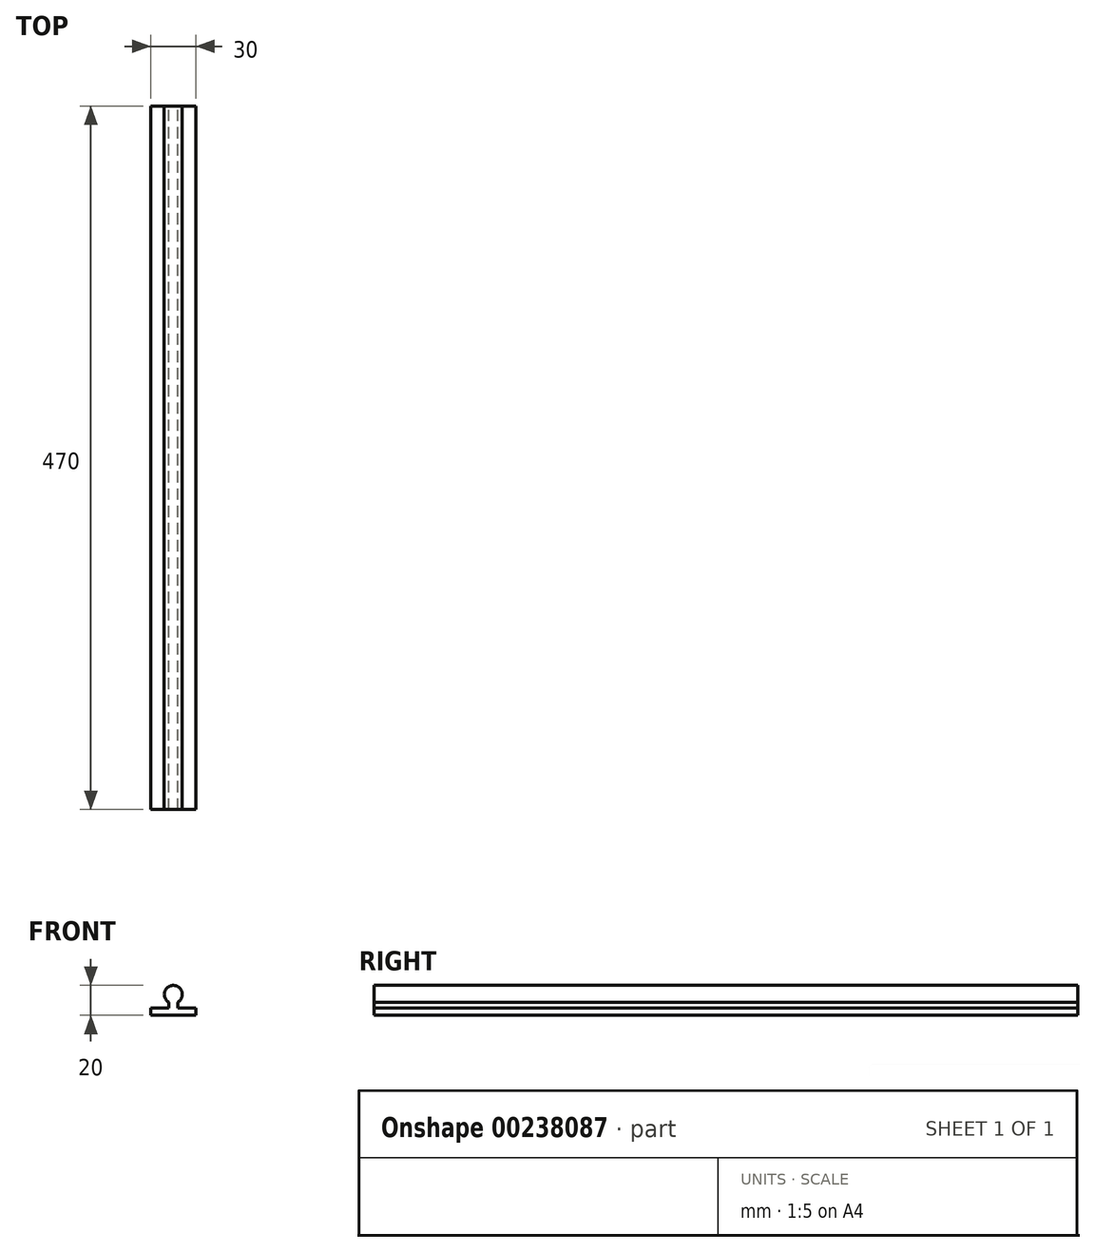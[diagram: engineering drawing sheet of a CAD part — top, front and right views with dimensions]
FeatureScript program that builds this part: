
annotation { "Feature Type Name" : "Feature", "Feature Type Description" : "" }
export const myFeature = defineFeature(function(context is Context, id is Id, definition is map)
    precondition{}
    {
        {
            var Q0;
            Q0=qCreatedBy(makeId("Front.planeOp"),FACE);
            var sketch = newSketch(context, id + "F0", { "sketchPlane" : qUnion([Q0])});
            skLineSegment(sketch, "E0", {"start": v(0, 0) * mm, "end": v(-15, 0) * mm});
            skLineSegment(sketch, "E1", {"start": v(-15, 0) * mm, "end": v(-15, 5) * mm});
            skLineSegment(sketch, "E2", {"start": v(-15, 5) * mm, "end": v(-3, 5) * mm});
            skArc(sketch, "E3", {"start": v(0, 20) * mm, "mid": v(-5.8, 15.55) * mm, "end": v(-3, 8.8) * mm});
            skLineSegment(sketch, "E4", {"start": v(-3, 5) * mm, "end": v(-3, 8.8) * mm});
            skPoint(sketch, "E5.start.orphan", {"position": v(0, 5) * mm});
            skLineSegment(sketch, "E6.MirrorCS", {"start": v(3, 5) * mm, "end": v(3, 8.8) * mm});
            skLineSegment(sketch, "E7.MirrorCS", {"start": v(15, 0) * mm, "end": v(15, 5) * mm});
            skLineSegment(sketch, "E8.MirrorCS", {"start": v(15, 5) * mm, "end": v(3, 5) * mm});
            skLineSegment(sketch, "E9.MirrorCS", {"start": v(0, 0) * mm, "end": v(15, 0) * mm});
            skArc(sketch, "E10.MirrorCS", {"start": v(0, 20) * mm, "mid": v(5.8, 15.55) * mm, "end": v(3, 8.8) * mm});
            skSolve(sketch);
        }
        {
            var Q0;
            Q0=makeQuery(id+"F0.imprint","IMPRINT",FACE,{"disambiguationData":[TD([[makeQuery(id+"F0.imprint","IMPRINT",EDGE,{"derivedFrom":sQuery(id+"F0.wireOp",EDGE,"E0")}),-1.0]])]});
            extrude(context, id + "F1", {"entities" : qUnion([Q0]), "depth" : 470 * mm});
        }
    });
